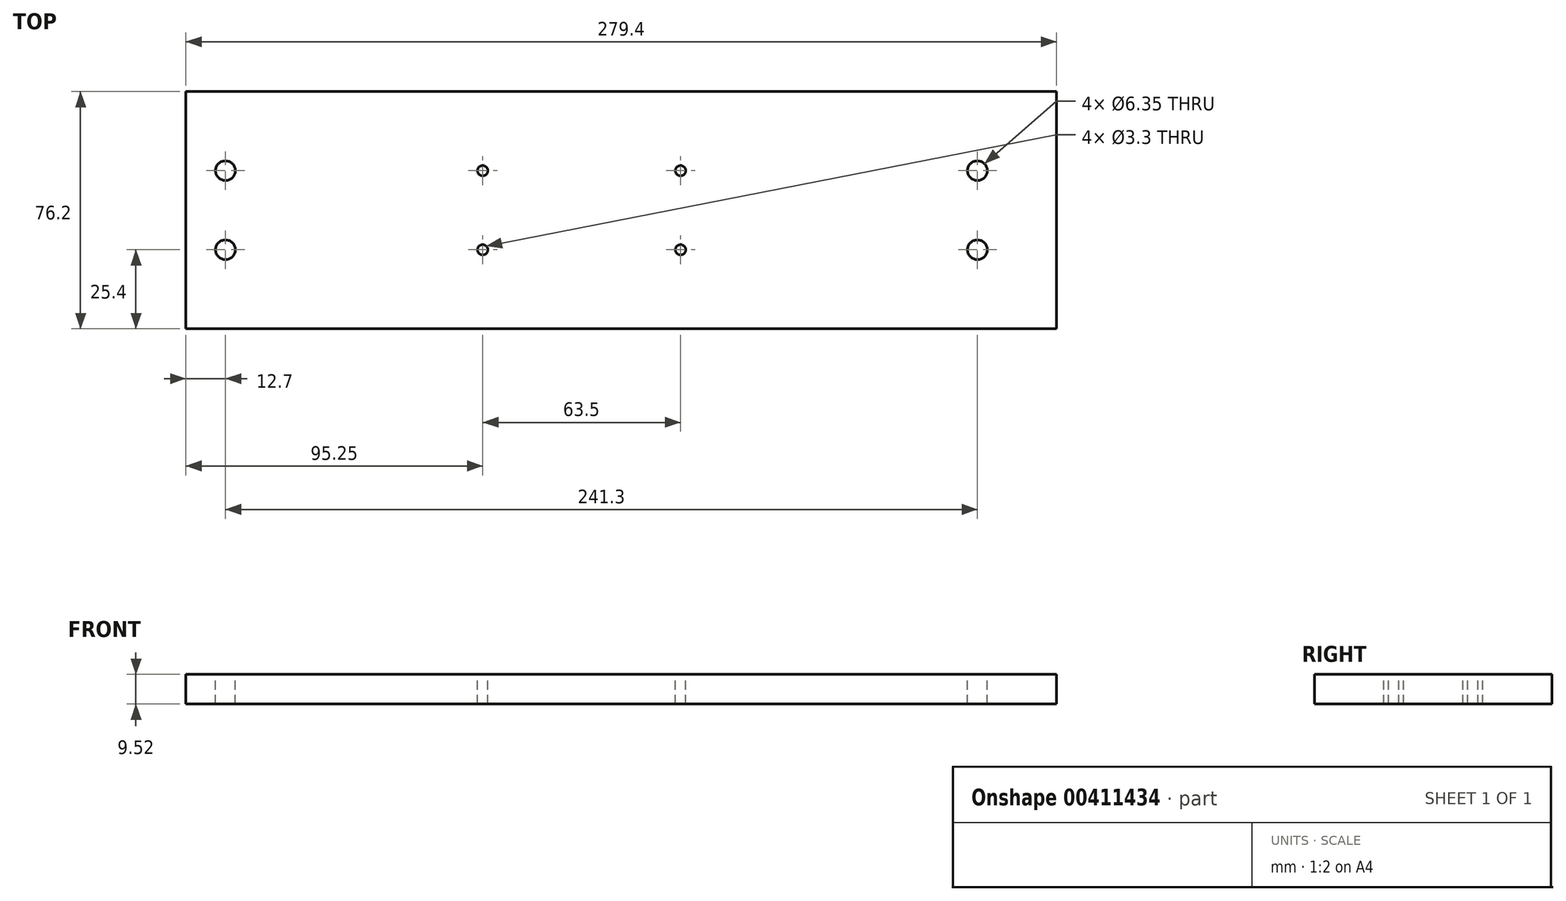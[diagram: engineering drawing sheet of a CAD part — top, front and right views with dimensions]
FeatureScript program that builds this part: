
annotation { "Feature Type Name" : "Feature", "Feature Type Description" : "" }
export const myFeature = defineFeature(function(context is Context, id is Id, definition is map)
    precondition{}
    {
        {
            var Q0;
            Q0=qCreatedBy(makeId("Front.planeOp"),FACE);
            var sketch = newSketch(context, id + "F0", { "sketchPlane" : qUnion([Q0])});
            skLineSegment(sketch, "E0.bottom", {"start": v(127, -4.76) * mm, "end": v(-152.4, -4.76) * mm});
            skLineSegment(sketch, "E0.top", {"start": v(127, 4.76) * mm, "end": v(-152.4, 4.76) * mm});
            skLineSegment(sketch, "E0.left", {"start": v(127, -4.76) * mm, "end": v(127, 4.76) * mm});
            skLineSegment(sketch, "E0.right", {"start": v(-152.4, -4.76) * mm, "end": v(-152.4, 4.76) * mm});
            skSolve(sketch);
        }
        {
            var Q0;
            Q0 = qSketchRegion(id + "F0", true);
            extrude(context, id + "F1", {"entities" : qUnion([Q0]), "endBound" : BoundingType.SYMMETRIC, "depth" : 76.2 * mm});
        }
        {
            var Q0;
            Q0=makeQuery(id+"F1.opExtrude","SWEPT_FACE",FACE,{"disambiguationData":[OSD([sQuery(id+"F0.wireOp",EDGE,"E0.top")])]});
            var sketch = newSketch(context, id + "F2", { "sketchPlane" : qUnion([Q0])});
            skCircle(sketch, "E1", {"center": v(-139.7, 12.7) * mm, "radius": 3.18 * mm});
            skCircle(sketch, "E2", {"center": v(-139.7, -12.7) * mm, "radius": 3.18 * mm});
            skCircle(sketch, "E3", {"center": v(101.6, 12.7) * mm, "radius": 3.18 * mm});
            skCircle(sketch, "E4", {"center": v(101.6, -12.7) * mm, "radius": 3.18 * mm});
            skSolve(sketch);
        }
        {
            var Q0;
            Q0 = qSketchRegion(id + "F2", true);
            extrude(context, id + "F3", {"entities" : qUnion([Q0]), "operationType" : NewBodyOperationType.REMOVE, "endBound" : BoundingType.SYMMETRIC, "oppositeDirection" : true, "depth" : 508 * mm});
        }
        {
            var Q0;
            Q0=makeQuery(id+"F1.opExtrude","SWEPT_FACE",FACE,{"disambiguationData":[OSD([sQuery(id+"F0.wireOp",EDGE,"E0.top")])]});
            var sketch = newSketch(context, id + "F4", { "sketchPlane" : qUnion([Q0])});
            skCircle(sketch, "E5", {"center": v(-57.15, 12.7) * mm, "radius": 1.65 * mm});
            skCircle(sketch, "E6", {"center": v(-57.15, -12.7) * mm, "radius": 1.65 * mm});
            skCircle(sketch, "E7", {"center": v(6.35, -12.7) * mm, "radius": 1.65 * mm});
            skCircle(sketch, "E8", {"center": v(6.35, 12.7) * mm, "radius": 1.65 * mm});
            skSolve(sketch);
        }
        {
            var Q0;
            Q0 = qSketchRegion(id + "F4", true);
            extrude(context, id + "F5", {"entities" : qUnion([Q0]), "operationType" : NewBodyOperationType.REMOVE, "endBound" : BoundingType.SYMMETRIC, "oppositeDirection" : true, "depth" : 508 * mm});
        }
    });
